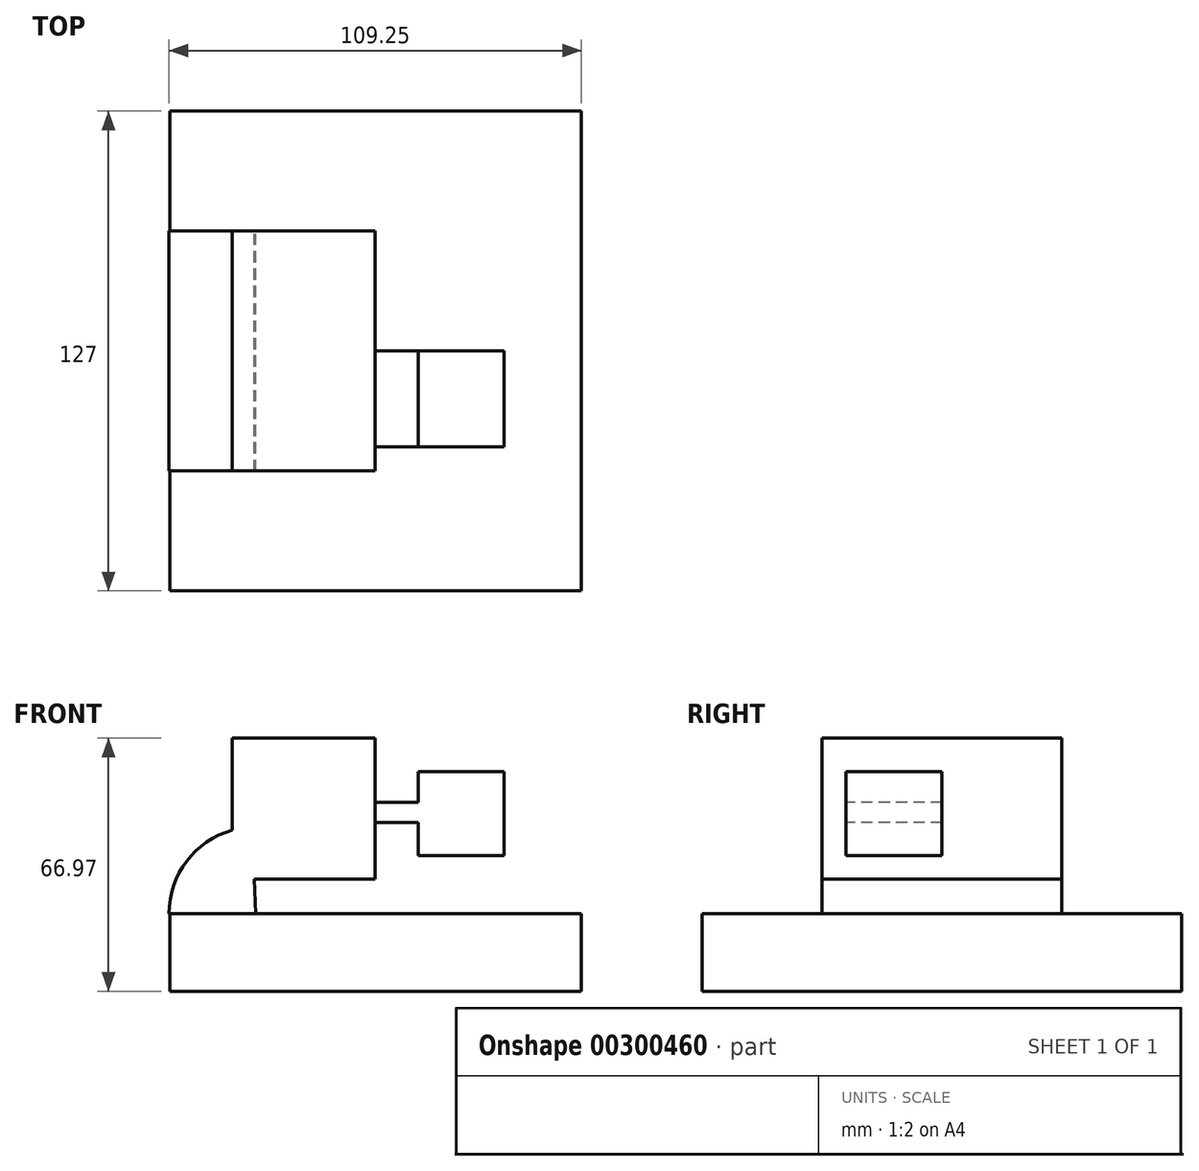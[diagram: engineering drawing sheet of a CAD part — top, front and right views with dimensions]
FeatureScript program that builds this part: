
annotation { "Feature Type Name" : "Feature", "Feature Type Description" : "" }
export const myFeature = defineFeature(function(context is Context, id is Id, definition is map)
    precondition{}
    {
        {
            var Q0;
            Q0=qCreatedBy(makeId("Front.planeOp"),FACE);
            var sketch = newSketch(context, id + "F0", { "sketchPlane" : qUnion([Q0])});
            skLineSegment(sketch, "E0.bottom", {"start": v(-35.83, -41.12) * mm, "end": v(71.66, -41.12) * mm});
            skLineSegment(sketch, "E0.top", {"start": v(-35.83, -63.73) * mm, "end": v(71.66, -63.73) * mm});
            skLineSegment(sketch, "E0.left", {"start": v(-35.83, -41.12) * mm, "end": v(-35.83, -63.73) * mm});
            skLineSegment(sketch, "E0.right", {"start": v(71.66, -41.12) * mm, "end": v(71.66, -63.73) * mm});
            skLineSegment(sketch, "E1.bottom", {"start": v(-19.1, 5.29) * mm, "end": v(18.8, 5.29) * mm});
            skLineSegment(sketch, "E1.top", {"start": v(-19.1, -32.01) * mm, "end": v(18.8, -32.01) * mm});
            skLineSegment(sketch, "E1.left", {"start": v(-19.1, 5.29) * mm, "end": v(-19.1, -32.01) * mm});
            skLineSegment(sketch, "E1.right", {"start": v(18.8, 5.29) * mm, "end": v(18.8, -32.01) * mm});
            skArc(sketch, "E2", {"start": v(-19.1, -19.05) * mm, "mid": v(-31.17, -27.27) * mm, "end": v(-35.83, -41.12) * mm});
            skLineSegment(sketch, "E3", {"start": v(-13.22, -32.01) * mm, "end": v(-12.92, -41.12) * mm});
            skPoint(sketch, "E4.firstSnap0", {"position": v(18.8, -13.36) * mm});
            skLineSegment(sketch, "E4.bottom", {"start": v(10.57, -13.36) * mm, "end": v(38.47, -13.36) * mm});
            skLineSegment(sketch, "E4.top", {"start": v(10.57, -20.56) * mm, "end": v(38.47, -20.56) * mm});
            skLineSegment(sketch, "E4.left", {"start": v(10.57, -13.36) * mm, "end": v(10.57, -20.56) * mm});
            skLineSegment(sketch, "E4.right", {"start": v(38.47, -13.36) * mm, "end": v(38.47, -20.56) * mm});
            skLineSegment(sketch, "E5.bottom", {"start": v(33.77, -2.64) * mm, "end": v(57.86, -2.64) * mm});
            skLineSegment(sketch, "E5.top", {"start": v(33.77, -27.02) * mm, "end": v(57.86, -27.02) * mm});
            skLineSegment(sketch, "E5.left", {"start": v(33.77, -2.64) * mm, "end": v(33.77, -27.02) * mm});
            skLineSegment(sketch, "E5.right", {"start": v(57.86, -2.64) * mm, "end": v(57.86, -27.02) * mm});
            skSolve(sketch);
        }
        {
            var Q0;
            {var subQ1=sQuery(id+"F0.wireOp",EDGE,"E1.bottom");Q0=makeQuery(id+"F0.imprint","IMPRINT",FACE,{"disambiguationData":[TD([[makeQuery(id+"F0.imprint","IMPRINT",EDGE,{"derivedFrom":subQ1}),-1.0]])]});}
            var Q1;
            {var subQ5=sQuery(id+"F0.wireOp",EDGE,"E4.left");Q1=makeQuery(id+"F0.imprint","IMPRINT",FACE,{"disambiguationData":[TD([[makeQuery(id+"F0.imprint","IMPRINT",EDGE,{"derivedFrom":subQ5}),1.0]])]});}
            var Q2;
            {var subQ0=sQuery(id+"F0.wireOp",EDGE,"E2");Q2=makeQuery(id+"F0.imprint","IMPRINT",FACE,{"disambiguationData":[TD([[makeQuery(id+"F0.imprint","IMPRINT",EDGE,{"derivedFrom":subQ0}),1.0]])]});}
            extrude(context, id + "F1", {"entities" : qUnion([Q0, Q1, Q2]), "endBound" : BoundingType.SYMMETRIC, "depth" : 63.5 * mm});
        }
        {
            var Q0;
            Q0=qCreatedBy(makeId("Front.planeOp"),FACE);
            var sketch = newSketch(context, id + "F2", { "sketchPlane" : qUnion([Q0])});
            skLineSegment(sketch, "E6.bottom", {"start": v(-35.54, -41.12) * mm, "end": v(73.42, -41.12) * mm});
            skLineSegment(sketch, "E6.top", {"start": v(-35.54, -61.68) * mm, "end": v(73.42, -61.68) * mm});
            skLineSegment(sketch, "E6.left", {"start": v(-35.54, -41.12) * mm, "end": v(-35.54, -61.68) * mm});
            skLineSegment(sketch, "E6.right", {"start": v(73.42, -41.12) * mm, "end": v(73.42, -61.68) * mm});
            skSolve(sketch);
        }
        {
            var Q0;
            Q0 = qSketchRegion(id + "F2", true);
            extrude(context, id + "F3", {"entities" : qUnion([Q0]), "operationType" : NewBodyOperationType.ADD, "endBound" : BoundingType.SYMMETRIC, "depth" : 127 * mm});
        }
        {
            var Q0;
            Q0=qCreatedBy(makeId("Front.planeOp"),FACE);
            var sketch = newSketch(context, id + "F4", { "sketchPlane" : qUnion([Q0])});
            skLineSegment(sketch, "E7.bottom", {"start": v(17.03, -11.75) * mm, "end": v(30.84, -11.75) * mm});
            skLineSegment(sketch, "E7.top", {"start": v(17.03, -17.03) * mm, "end": v(30.84, -17.03) * mm});
            skLineSegment(sketch, "E7.left", {"start": v(17.03, -11.75) * mm, "end": v(17.03, -17.03) * mm});
            skLineSegment(sketch, "E7.right", {"start": v(30.84, -11.75) * mm, "end": v(30.84, -17.03) * mm});
            skLineSegment(sketch, "E8.bottom", {"start": v(30.25, -3.52) * mm, "end": v(52.86, -3.52) * mm});
            skLineSegment(sketch, "E8.top", {"start": v(30.25, -25.85) * mm, "end": v(52.86, -25.85) * mm});
            skLineSegment(sketch, "E8.left", {"start": v(30.25, -3.52) * mm, "end": v(30.25, -25.85) * mm});
            skLineSegment(sketch, "E8.right", {"start": v(52.86, -3.52) * mm, "end": v(52.86, -25.85) * mm});
            skSolve(sketch);
        }
        {
            var Q0;
            Q0 = qSketchRegion(id + "F4", true);
            extrude(context, id + "F5", {"entities" : qUnion([Q0]), "operationType" : NewBodyOperationType.ADD, "depth" : 25.4 * mm});
        }
    });
